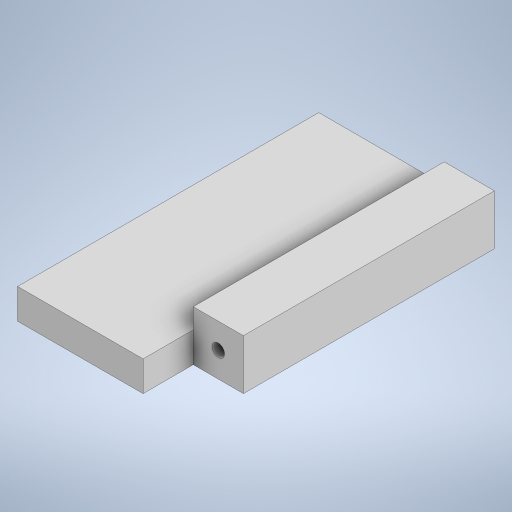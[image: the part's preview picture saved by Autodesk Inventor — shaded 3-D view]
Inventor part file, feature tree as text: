
AUTODESK INVENTOR PART (.ipt)
format: ipt  version: 2023 (Build 270158000, 158)  size: 246,784 bytes
history: native  units: in
note: dims shown in document units (in); Inventor stores cm internally (conversion verified against a paired STEP export)
features: extrude x4, sketch x4
ambient origin geometry x8: Origin, YZ Plane, XZ Plane, XY Plane, X Axis, Y Axis, Z Axis, Center Point
bodies: Body1 (feature_tree)
feature tree (8):
  extrude  "Extrusion2"  Depth=0.7874in
  extrude  "Extrusion4"  Depth=0.3937in
  extrude  "Extrusion5"  Depth=0.9843in TaperAngle=0.0deg
  extrude  "Extrusion6"  Depth=1.9685in
  sketch  "Sketch1"  dims[d0=0.7874in d1=0.7874in]
  sketch  "Sketch4"  dims[d5=0.3937in d6=0.3937in]
  sketch  "Sketch5"  dims[d7=0.1969in d8=0.9843in d9=0.0in]
  sketch  "Sketch6"  dims[d13=0.4724in d14=1.9685in d15=3.937in d16=0.0in d17=0.3543in d18=2.9528in d19=0.0in d20=0.7874in d21=0.0in d22=0.0197in d23=0.0344in]
